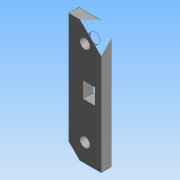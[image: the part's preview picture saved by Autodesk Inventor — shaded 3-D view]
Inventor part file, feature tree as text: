
AUTODESK INVENTOR PART (.ipt)
format: ipt  version: 2015 (Build 190159000, 159)  size: 95,232 bytes
history: native  units: mm
features: extrude x2, sketch x2
ambient origin geometry x8: Origin, YZ Plane, XZ Plane, XY Plane, X Axis, Y Axis, Z Axis, Center Point
bodies: Solid1 (feature_tree)
feature tree (4):
  extrude  "Extrusion1"  Depth=60.0mm
  extrude  "Extrusion2"  Depth=8.0mm
  sketch  "Sketch1"  dims[d0=5.0mm d1=0.0mm d2=60.0mm]
  sketch  "Sketch2"  dims[d3=16.0mm d4=8.0mm d5=5.0mm d6=9.0mm d7=8.0mm d8=9.0mm d9=5.0mm d10=8.0mm d11=6.0mm d12=7.0mm d13=25.0mm d14=10.0mm d15=0.0mm]
